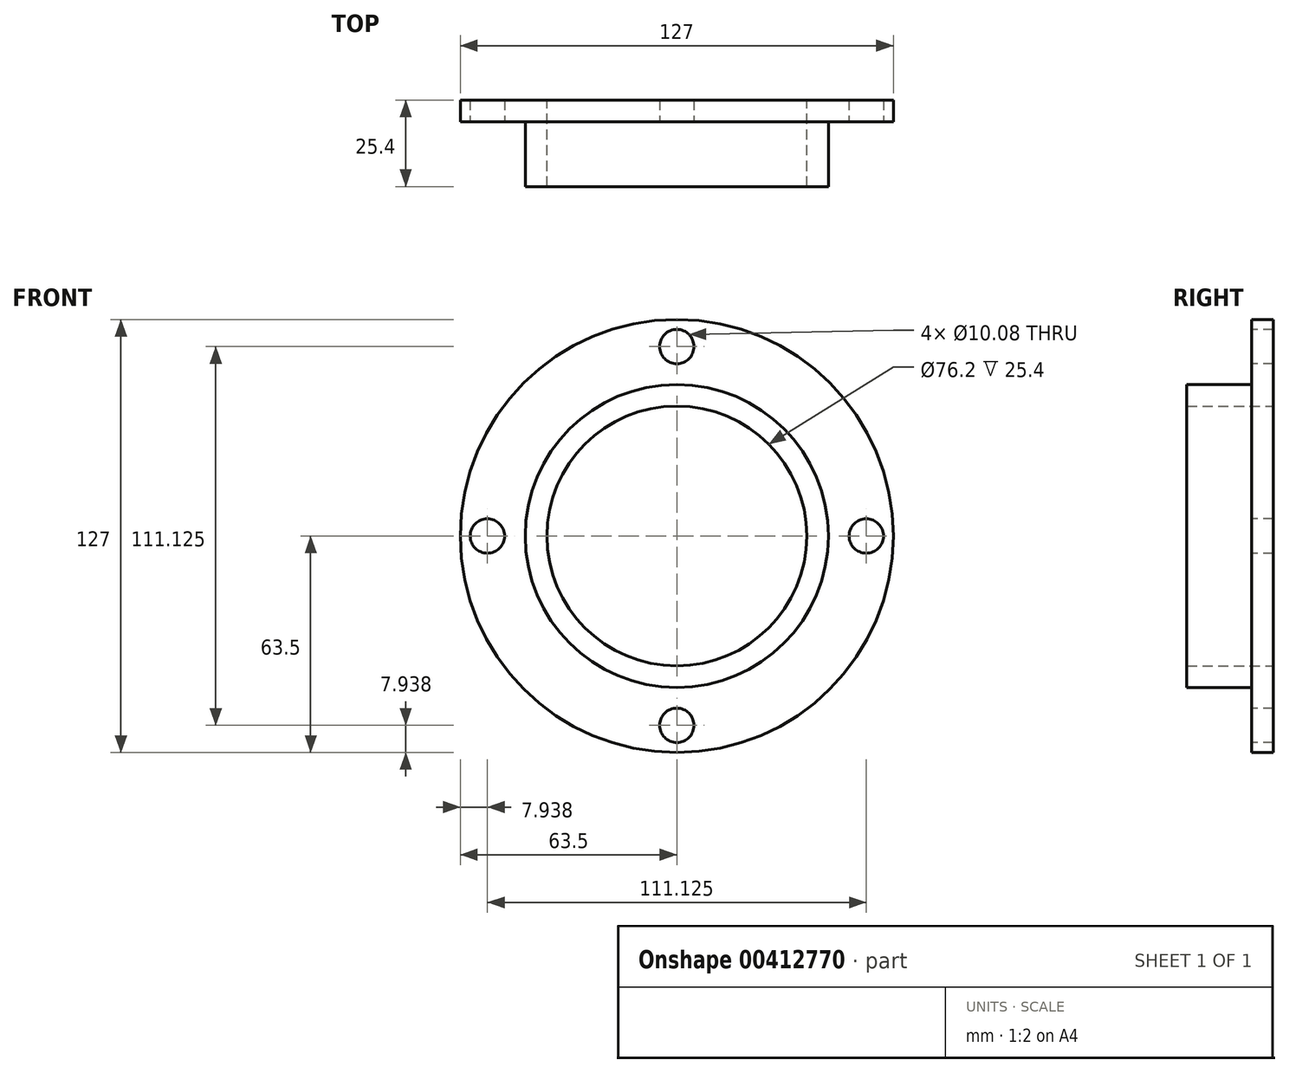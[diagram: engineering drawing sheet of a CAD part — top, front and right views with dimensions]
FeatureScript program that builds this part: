
annotation { "Feature Type Name" : "Feature", "Feature Type Description" : "" }
export const myFeature = defineFeature(function(context is Context, id is Id, definition is map)
    precondition{}
    {
        {
            var Q0;
            Q0=qCreatedBy(makeId("Front.planeOp"),FACE);
            var sketch = newSketch(context, id + "F0", { "sketchPlane" : qUnion([Q0])});
            skCircle(sketch, "E0", {"center": v(0, 0) * mm, "radius": 38.1 * mm});
            skCircle(sketch, "E1", {"center": v(0, 0) * mm, "radius": 63.5 * mm});
            skSolve(sketch);
        }
        {
            var Q0;
            Q0 = qSketchRegion(id + "F0", true);
            extrude(context, id + "F1", {"entities" : qUnion([Q0]), "depth" : 6.35 * mm, "offsetDistance" : 25.4 * mm});
        }
        {
            var Q0;
            Q0=makeQuery(id+"F1.opExtrude","CAP_FACE",FACE,{"disambiguationData":[OSD([sQuery(id+"F0.wireOp",EDGE,"E0"),sQuery(id+"F0.wireOp",EDGE,"E1")])],"isStart":false});
            var sketch = newSketch(context, id + "F2", { "sketchPlane" : qUnion([Q0])});
            skCircle(sketch, "E2", {"center": v(0, 0) * mm, "radius": 44.45 * mm});
            skCircle(sketch, "E3", {"center": v(0, 0) * mm, "radius": 38.1 * mm});
            skSolve(sketch);
        }
        {
            var Q0;
            Q0 = qSketchRegion(id + "F2", true);
            extrude(context, id + "F3", {"entities" : qUnion([Q0]), "operationType" : NewBodyOperationType.ADD, "depth" : 19.05 * mm, "offsetDistance" : 25.4 * mm});
        }
        {
            var Q0;
            Q0=makeQuery(id+"F1.opExtrude","CAP_FACE",FACE,{"disambiguationData":[OSD([sQuery(id+"F0.wireOp",EDGE,"E0"),sQuery(id+"F0.wireOp",EDGE,"E1")])],"isStart":false});
            var sketch = newSketch(context, id + "F4", { "sketchPlane" : qUnion([Q0])});
            skCircle(sketch, "E4", {"center": v(0, 0) * mm, "radius": 55.56 * mm, "construction": true});
            skPoint(sketch, "E5", {"position": v(0, 55.56) * mm});
            skPoint(sketch, "E6", {"position": v(55.56, 0) * mm});
            skPoint(sketch, "E7", {"position": v(0, -55.56) * mm});
            skPoint(sketch, "E8", {"position": v(-55.56, 0) * mm});
            skSolve(sketch);
        }
        {
            var Q0;
            Q0=sQuery(id+"F4.wireOp",VERTEX,"E5");
            var Q1;
            Q1=sQuery(id+"F4.wireOp",VERTEX,"E6");
            var Q2;
            Q2=sQuery(id+"F4.wireOp",VERTEX,"E8");
            var Q3;
            Q3=sQuery(id+"F4.wireOp",VERTEX,"E7");
            var Q4;
            Q4=makeQuery(id+"F1.opExtrude","SWEPT_BODY",BODY,{"disambiguationData":[OSD([sQuery(id+"F0.wireOp",EDGE,"E0"),sQuery(id+"F0.wireOp",EDGE,"E1")])]});
            hole(context, id + "F5", {"style" : HoleStyle.SIMPLE, "endStyle" : HoleEndStyle.THROUGH, "standardTappedOrClearance" : lookupTablePath({ "standard" : "ANSI", "fit" : "Normal (ASME)", "size" : "3/8", "type" : "Clearance" }), "standardBlindInLast" : lookupTablePath({ "fit" : "Free", "standard" : "ANSI", "size" : "3/8", "type" : "Clearance" }), "holeDiameter" : 10.08 * mm, "tappedDepth" : 20.65 * mm, "tapClearance" : 3, "startFromSketch" : true, "locations" : qUnion([Q0, Q1, Q2, Q3]), "scope" : qUnion([Q4])});
        }
    });
